# Revit family: KLVL276NB
name_source: partatom
category: Lighting Fixtures
revit_build: Autodesk Revit 2014 (Build: 20130308_1515(x64)
units: mm (PartAtom-declared; Revit-internal decimal feet)

## types (3) — shared parameters
Apparent Load = 0 VA
Assembly Code = D5020200
Color Filter = 16777215
Description = Ravenna Lowlighter is highly adaptable to landscape accent lighting solutions. Elegance and style in leaf-like design blends into natural surroundings.
Diameter = 5 "
Dimming Lamp Color Temperature Shift = <None>
Glass = Glass-KIM-Temper Molded
Height = 24 "
Lamp = LED
Load Classification = Lighting
Manufacturer = Kim Lighting
MasterFormat Title = Landscape Lighting, Site Lighting, Walkway Lighting
Model = Ravenna Lowlighter
Number of Poles = 1
Photometric Notes = More IES files download on Photometric Web Link
Photometric Web File = klvl276-3l3k.ies
Photometric Web Link = https://www.hubbell.com
Power Factor = 1
Product Documentation Link = https://hubbellcdn.com
Product Page URL = https://www.hubbell.com
Series = Landscape
Tilt Angle = 90.00°
Type Comments = landscape path light
URL = https://www.hubbell.com
Voltage = 120 V
Warranty = For full warranty see http://www.hubbelllighting.
com/resources/warranty
Wattage Comments = default
Width = 5.31 "

## per-type parameters (varying)
| type | Finish |
| ELL271DB | Powder Coat-Kim-Dark Bronze |
| ELL271BL | Powder Coat-Kim-Black |
| ELL271GR | Paint - Hubbell - Green Textured |

## geometry (parser evidence)
native form markers: Sweep x2
no freeform markers — native parametric forms only
